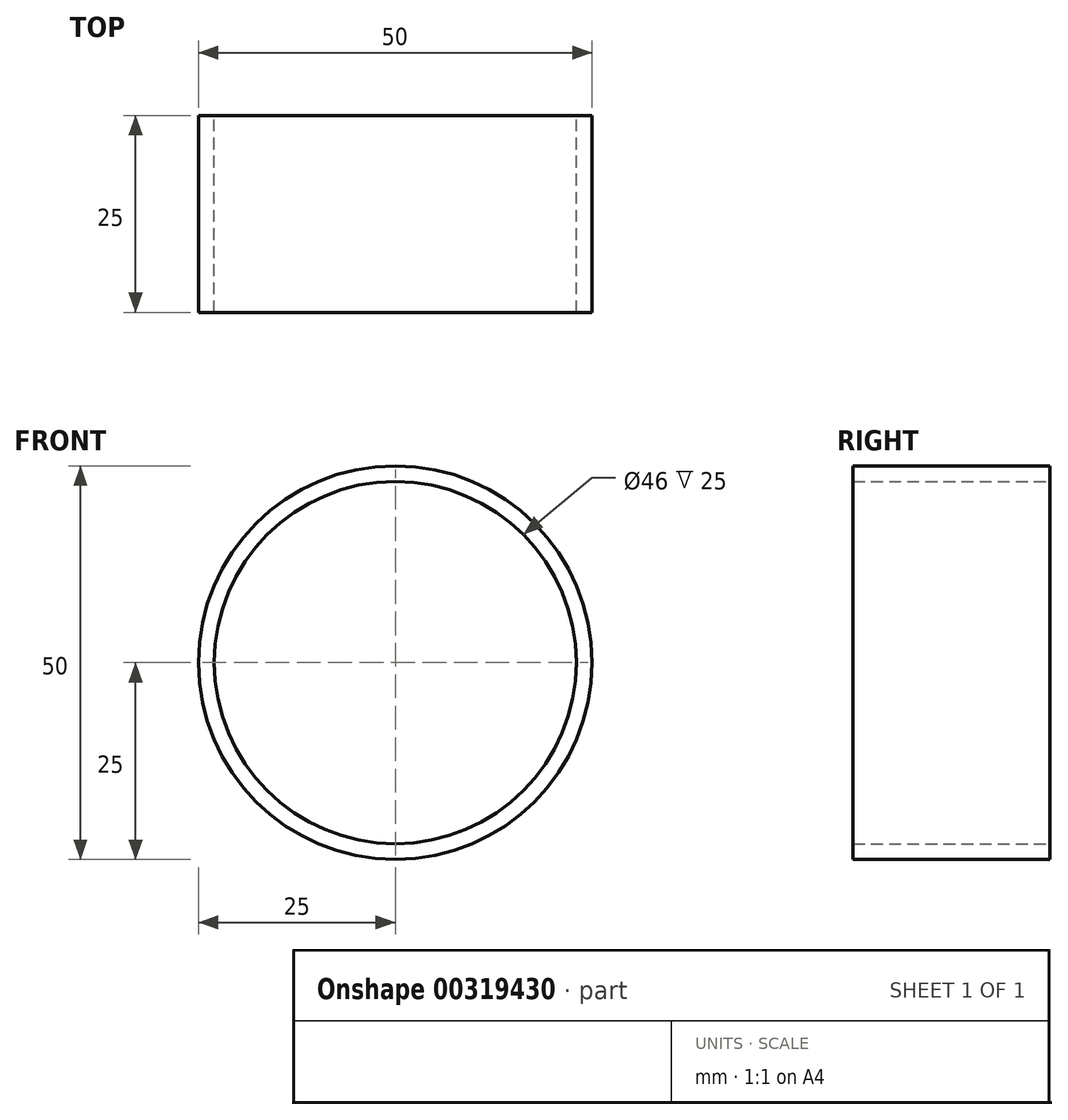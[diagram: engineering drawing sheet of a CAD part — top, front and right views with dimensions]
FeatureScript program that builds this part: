
annotation { "Feature Type Name" : "Feature", "Feature Type Description" : "" }
export const myFeature = defineFeature(function(context is Context, id is Id, definition is map)
    precondition{}
    {
        {
            var Q0;
            Q0=qCreatedBy(makeId("Front.planeOp"),FACE);
            var sketch = newSketch(context, id + "F0", { "sketchPlane" : qUnion([Q0])});
            skCircle(sketch, "E0", {"center": v(0, 0) * mm, "radius": 25 * mm});
            skCircle(sketch, "E1", {"center": v(0, 0) * mm, "radius": 23 * mm});
            skSolve(sketch);
        }
        {
            var Q0;
            Q0 = qSketchRegion(id + "F0", true);
            extrude(context, id + "F1", {"entities" : qUnion([Q0]), "depth" : 25 * mm});
        }
    });
